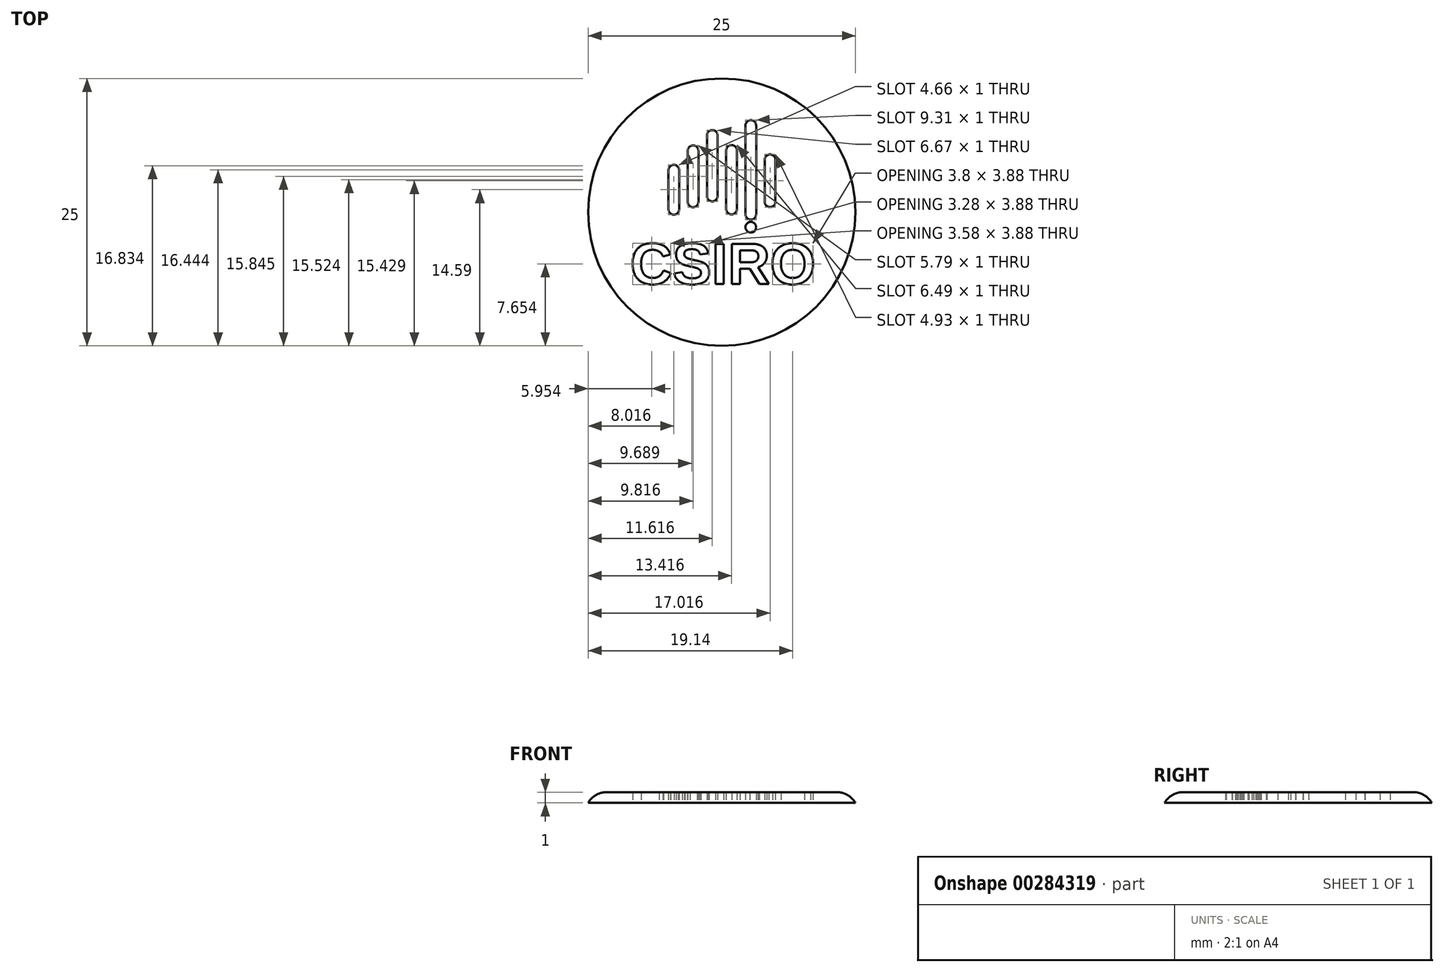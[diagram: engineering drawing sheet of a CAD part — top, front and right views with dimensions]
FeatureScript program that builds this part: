
annotation { "Feature Type Name" : "Feature", "Feature Type Description" : "" }
export const myFeature = defineFeature(function(context is Context, id is Id, definition is map)
    precondition{}
    {
        {
            var Q0;
            Q0=qCreatedBy(makeId("Top.planeOp"),FACE);
            var sketch = newSketch(context, id + "F0", { "sketchPlane" : qUnion([Q0])});
            skCircle(sketch, "E0", {"center": v(0, 0) * mm, "radius": 12.5 * mm});
            skSolve(sketch);
        }
        {
            var Q0;
            Q0=makeQuery(id+"F0.imprint","IMPRINT",FACE,{"disambiguationData":[TD([[makeQuery(id+"F0.imprint","IMPRINT",EDGE,{"derivedFrom":sQuery(id+"F0.wireOp",EDGE,"E0")}),1.0]])]});
            extrude(context, id + "F1", {"entities" : qUnion([Q0]), "depth" : 1 * mm});
        }
        {
            var Q0;
            Q0=makeQuery(id+"F1.opExtrude","CAP_EDGE",EDGE,{"disambiguationData":[OSD([sQuery(id+"F0.wireOp",EDGE,"E0")])],"isStart":false});
            fillet(context, id + "F2", {"entities" : qUnion([Q0]), "radius" : 2 * mm, "tangentPropagation" : true, "allowEdgeOverflow" : false});
        }
        {
            var Q0;
            Q0=qCreatedBy(makeId("Top.planeOp"),FACE);
            var sketch = newSketch(context, id + "F3", { "sketchPlane" : qUnion([Q0])});
            skText(sketch, "E1", { "text": "CSIRO", "fontName": "Arimo-Bold.ttf"});
            const initialGuessF3  = {"E1": [-0.00856, -0.00673, 1, 0, 0.00394]};
            skSetInitialGuess(sketch, initialGuessF3);
            skSolve(sketch);
        }
        {
            var Q0;
            Q0=qSketchRegion(id+"F3",true);
            extrude(context, id + "F4", {"entities" : qUnion([Q0]), "operationType" : NewBodyOperationType.REMOVE, "depth" : 3 * mm});
        }
        {
            var Q0;
            Q0=qCreatedBy(makeId("Top.planeOp"),FACE);
            var sketch = newSketch(context, id + "F5", { "sketchPlane" : qUnion([Q0])});
            skArc(sketch, "E2", {"start": v(-3.98, 3.92) * mm, "mid": v(-4.48, 4.42) * mm, "end": v(-4.98, 3.92) * mm});
            skArc(sketch, "E3", {"start": v(-4.98, 0.26) * mm, "mid": v(-4.48, -0.24) * mm, "end": v(-3.98, 0.26) * mm});
            skLineSegment(sketch, "E4", {"start": v(-3.98, 0.26) * mm, "end": v(-3.98, 3.92) * mm});
            skLineSegment(sketch, "E5.MirrorCS", {"start": v(-4.98, 0.26) * mm, "end": v(-4.98, 3.92) * mm});
            skArc(sketch, "E6.1.0.0", {"start": v(-3.18, 0.95) * mm, "mid": v(-2.68, 0.45) * mm, "end": v(-2.18, 0.95) * mm});
            skLineSegment(sketch, "E6.1.0.1", {"start": v(-2.18, 0.95) * mm, "end": v(-2.18, 5.74) * mm});
            skLineSegment(sketch, "E6.1.0.2", {"start": v(-3.18, 0.95) * mm, "end": v(-3.18, 5.74) * mm});
            skArc(sketch, "E6.1.0.3", {"start": v(-2.18, 5.74) * mm, "mid": v(-2.68, 6.24) * mm, "end": v(-3.18, 5.74) * mm});
            skArc(sketch, "E6.2.0.0", {"start": v(-1.38, 1.5) * mm, "mid": v(-0.88, 1) * mm, "end": v(-0.38, 1.5) * mm});
            skLineSegment(sketch, "E6.2.0.1", {"start": v(-0.38, 1.5) * mm, "end": v(-0.38, 7.17) * mm});
            skLineSegment(sketch, "E6.2.0.2", {"start": v(-1.38, 1.5) * mm, "end": v(-1.38, 7.17) * mm});
            skArc(sketch, "E6.2.0.3", {"start": v(-0.38, 7.17) * mm, "mid": v(-0.88, 7.67) * mm, "end": v(-1.38, 7.17) * mm});
            skArc(sketch, "E6.3.0.0", {"start": v(0.42, 0.28) * mm, "mid": v(0.92, -0.22) * mm, "end": v(1.42, 0.28) * mm});
            skLineSegment(sketch, "E6.3.0.1", {"start": v(1.42, 0.28) * mm, "end": v(1.42, 5.77) * mm});
            skLineSegment(sketch, "E6.3.0.2", {"start": v(0.42, 0.28) * mm, "end": v(0.42, 5.77) * mm});
            skArc(sketch, "E6.3.0.3", {"start": v(1.42, 5.77) * mm, "mid": v(0.92, 6.27) * mm, "end": v(0.42, 5.77) * mm});
            skArc(sketch, "E6.4.0.0", {"start": v(2.22, -0.2) * mm, "mid": v(2.72, -0.7) * mm, "end": v(3.22, -0.2) * mm});
            skLineSegment(sketch, "E6.4.0.1", {"start": v(3.22, -0.2) * mm, "end": v(3.22, 8.1) * mm});
            skLineSegment(sketch, "E6.4.0.2", {"start": v(2.22, -0.2) * mm, "end": v(2.22, 8.1) * mm});
            skArc(sketch, "E6.4.0.3", {"start": v(3.22, 8.1) * mm, "mid": v(2.72, 8.6) * mm, "end": v(2.22, 8.1) * mm});
            skArc(sketch, "E6.5.0.0", {"start": v(4.02, 0.96) * mm, "mid": v(4.52, 0.46) * mm, "end": v(5.02, 0.96) * mm});
            skLineSegment(sketch, "E6.5.0.1", {"start": v(5.02, 0.96) * mm, "end": v(5.02, 4.9) * mm});
            skLineSegment(sketch, "E6.5.0.2", {"start": v(4.02, 0.96) * mm, "end": v(4.02, 4.9) * mm});
            skArc(sketch, "E6.5.0.3", {"start": v(5.02, 4.9) * mm, "mid": v(4.52, 5.4) * mm, "end": v(4.02, 4.9) * mm});
            skCircle(sketch, "E7", {"center": v(2.72, -1.41) * mm, "radius": 0.5 * mm});
            skSolve(sketch);
        }
        {
            var Q0;
            Q0=qSketchRegion(id+"F5",true);
            extrude(context, id + "F6", {"entities" : qUnion([Q0]), "operationType" : NewBodyOperationType.REMOVE, "depth" : 6.6 * mm});
        }
    });
